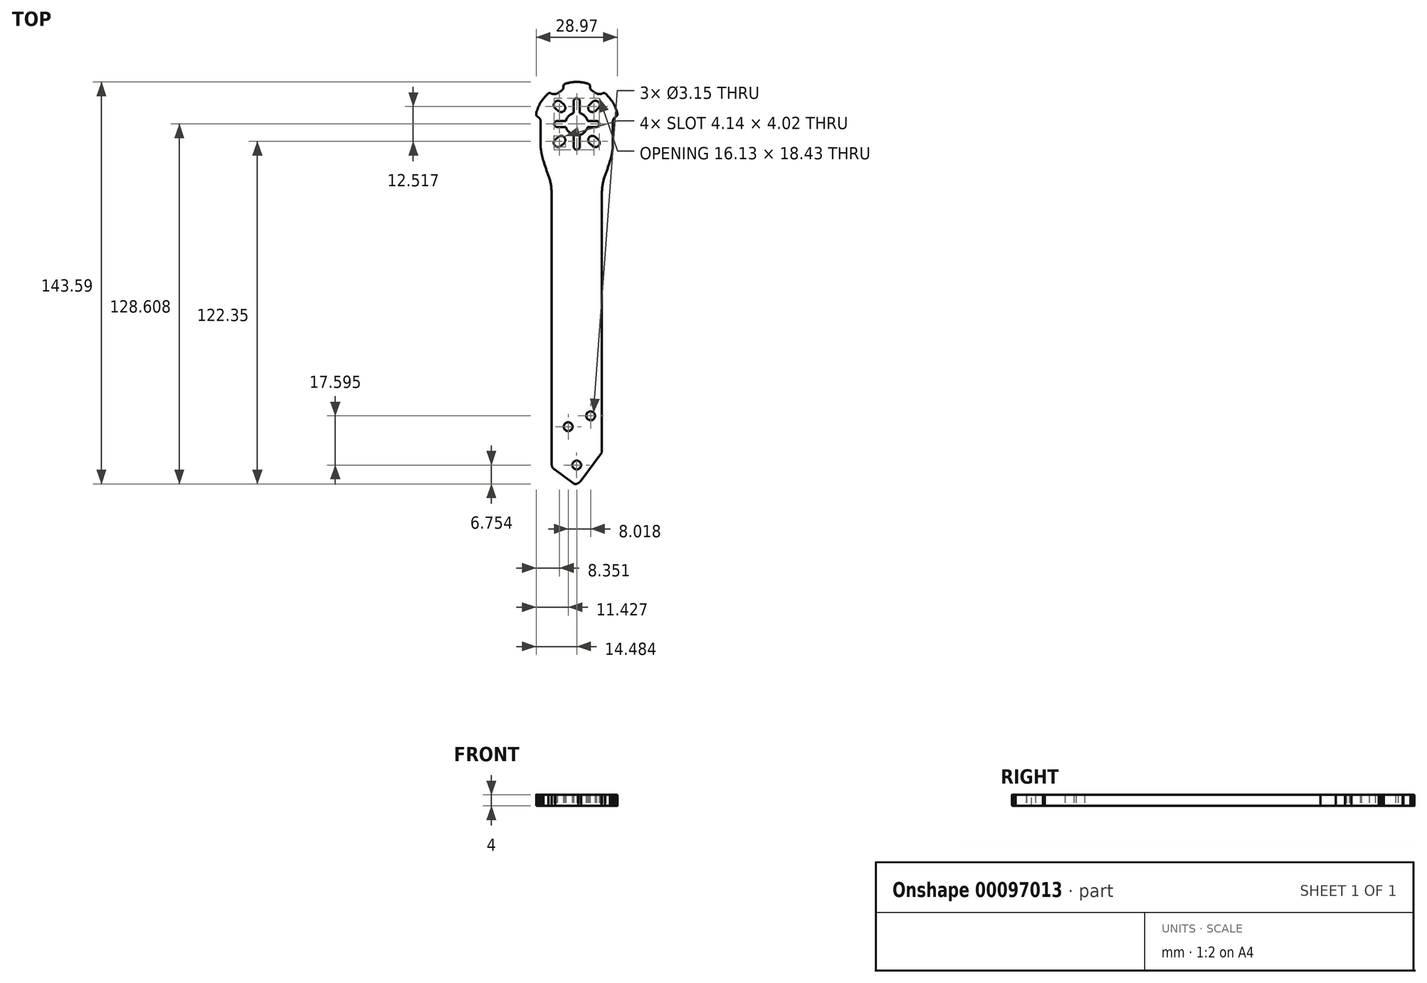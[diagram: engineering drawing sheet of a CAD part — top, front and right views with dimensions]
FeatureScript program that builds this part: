
annotation { "Feature Type Name" : "Feature", "Feature Type Description" : "" }
export const myFeature = defineFeature(function(context is Context, id is Id, definition is map)
    precondition{}
    {
        {
            var Q0;
            Q0=qCreatedBy(makeId("Top.planeOp"),FACE);
            var sketch = newSketch(context, id + "F0", { "sketchPlane" : qUnion([Q0])});
            skCircle(sketch, "E0", {"center": v(-4.22, -64.34) * mm, "radius": 1.57 * mm});
            skCircle(sketch, "E1", {"center": v(-12.24, -68.23) * mm, "radius": 1.57 * mm});
            skCircle(sketch, "E2", {"center": v(-9.2, -81.94) * mm, "radius": 1.57 * mm});
            skArc(sketch, "E3", {"start": v(-5.3, 41) * mm, "mid": v(-6.34, 42.79) * mm, "end": v(-8.13, 43.83) * mm});
            skArc(sketch, "E4", {"start": v(-1.12, 39.92) * mm, "mid": v(-1.4, 40.66) * mm, "end": v(-2.13, 41) * mm});
            skArc(sketch, "E5", {"start": v(-8.13, 48.05) * mm, "mid": v(-8.45, 48.82) * mm, "end": v(-9.22, 49.13) * mm});
            skLineSegment(sketch, "E6", {"start": v(-2.13, 41) * mm, "end": v(-5.3, 41) * mm});
            skLineSegment(sketch, "E7", {"start": v(-8.13, 48.05) * mm, "end": v(-8.13, 43.83) * mm});
            skLineSegment(sketch, "E8", {"start": v(-2.16, 45.18) * mm, "end": v(-2.16, 45.18) * mm});
            skArc(sketch, "E9", {"start": v(-4.61, 46.83) * mm, "mid": v(-4.74, 44.68) * mm, "end": v(-2.58, 44.55) * mm});
            skLineSegment(sketch, "E10", {"start": v(-3.52, 47.8) * mm, "end": v(-4.61, 46.83) * mm});
            skLineSegment(sketch, "E11", {"start": v(-2.58, 44.55) * mm, "end": v(-1.5, 45.52) * mm});
            skArc(sketch, "E12.trimOffspring", {"start": v(-1.5, 45.52) * mm, "mid": v(-1.37, 47.68) * mm, "end": v(-3.52, 47.8) * mm});
            skArc(sketch, "E13.MirrorCS", {"start": v(-1.5, 34.31) * mm, "mid": v(-1.37, 32.16) * mm, "end": v(-3.52, 32.03) * mm});
            skLineSegment(sketch, "E14.MirrorCS", {"start": v(-3.52, 32.03) * mm, "end": v(-4.61, 33) * mm});
            skArc(sketch, "E15.MirrorCS", {"start": v(-4.61, 33) * mm, "mid": v(-4.74, 35.16) * mm, "end": v(-2.58, 35.29) * mm});
            skLineSegment(sketch, "E16.MirrorCS", {"start": v(-2.58, 35.29) * mm, "end": v(-1.5, 34.31) * mm});
            skArc(sketch, "E17.MirrorCS", {"start": v(-1.12, 39.92) * mm, "mid": v(-1.4, 39.18) * mm, "end": v(-2.13, 38.84) * mm});
            skLineSegment(sketch, "E18.MirrorCS", {"start": v(-8.13, 31.79) * mm, "end": v(-8.13, 36) * mm});
            skLineSegment(sketch, "E19.MirrorCS", {"start": v(-2.13, 38.84) * mm, "end": v(-5.3, 38.84) * mm});
            skArc(sketch, "E20.MirrorCS", {"start": v(-5.3, 38.84) * mm, "mid": v(-6.34, 37.05) * mm, "end": v(-8.13, 36) * mm});
            skArc(sketch, "E21.MirrorCS", {"start": v(-8.13, 31.79) * mm, "mid": v(-8.45, 31.02) * mm, "end": v(-9.22, 30.7) * mm});
            skArc(sketch, "E22", {"start": v(0.93, 21.46) * mm, "mid": v(0.09, 18.5) * mm, "end": v(-0.19, 15.46) * mm});
            skArc(sketch, "E23", {"start": v(0.93, 21.46) * mm, "mid": v(1.86, 24.11) * mm, "end": v(2.71, 26.8) * mm});
            skArc(sketch, "E24", {"start": v(2.71, 26.8) * mm, "mid": v(3.17, 28.42) * mm, "end": v(3.5, 30.09) * mm});
            skArc(sketch, "E25", {"start": v(3.5, 30.09) * mm, "mid": v(3.66, 31.29) * mm, "end": v(3.74, 32.5) * mm});
            skLineSegment(sketch, "E26", {"start": v(3.74, 32.5) * mm, "end": v(3.74, 40.9) * mm});
            skArc(sketch, "E27", {"start": v(4.33, 42.17) * mm, "mid": v(3.9, 41.6) * mm, "end": v(3.74, 40.9) * mm});
            skArc(sketch, "E28", {"start": v(4.95, 42.62) * mm, "mid": v(4.64, 42.4) * mm, "end": v(4.33, 42.17) * mm});
            skArc(sketch, "E29", {"start": v(4.95, 42.62) * mm, "mid": v(5.2, 42.9) * mm, "end": v(5.3, 43.27) * mm});
            skArc(sketch, "E30", {"start": v(5.3, 43.27) * mm, "mid": v(5.28, 43.63) * mm, "end": v(5.2, 43.98) * mm});
            skArc(sketch, "E31", {"start": v(5.2, 43.98) * mm, "mid": v(3.66, 47.64) * mm, "end": v(1.1, 50.68) * mm});
            skArc(sketch, "E32", {"start": v(1.1, 50.68) * mm, "mid": v(0.6, 50.95) * mm, "end": v(0.04, 50.85) * mm});
            skArc(sketch, "E33", {"start": v(-2.22, 50.85) * mm, "mid": v(-1.09, 50.55) * mm, "end": v(0.04, 50.85) * mm});
            skArc(sketch, "E34", {"start": v(-4.01, 52.04) * mm, "mid": v(-3.15, 51.4) * mm, "end": v(-2.22, 50.85) * mm});
            skArc(sketch, "E35", {"start": v(-4.39, 52.76) * mm, "mid": v(-4.27, 52.36) * mm, "end": v(-4.01, 52.04) * mm});
            skArc(sketch, "E36", {"start": v(-4.45, 53.55) * mm, "mid": v(-4.42, 53.15) * mm, "end": v(-4.39, 52.76) * mm});
            skArc(sketch, "E37", {"start": v(-4.45, 53.55) * mm, "mid": v(-4.62, 53.95) * mm, "end": v(-4.96, 54.22) * mm});
            skArc(sketch, "E38", {"start": v(-4.96, 54.22) * mm, "mid": v(-7.06, 54.75) * mm, "end": v(-9.22, 54.9) * mm});
            skArc(sketch, "E39", {"start": v(-18.19, -81.72) * mm, "mid": v(-17.77, -82.83) * mm, "end": v(-16.92, -83.66) * mm});
            skLineSegment(sketch, "E40", {"start": v(-16.92, -83.66) * mm, "end": v(-10.54, -88.38) * mm});
            skArc(sketch, "E41", {"start": v(-10.54, -88.38) * mm, "mid": v(-9.6, -88.7) * mm, "end": v(-8.66, -88.38) * mm});
            skArc(sketch, "E42", {"start": v(-8.66, -88.38) * mm, "mid": v(-8.1, -87.97) * mm, "end": v(-7.64, -87.45) * mm});
            skLineSegment(sketch, "E43", {"start": v(-7.64, -87.45) * mm, "end": v(-0.42, -77.68) * mm});
            skArc(sketch, "E44", {"start": v(-0.42, -77.68) * mm, "mid": v(-0.26, -77.4) * mm, "end": v(-0.19, -77.07) * mm});
            skPoint(sketch, "E45", {"position": v(-9.19, 15.46) * mm});
            skLineSegment(sketch, "E46", {"start": v(-9.19, 54.9) * mm, "end": v(-9.19, -88.64) * mm});
            skArc(sketch, "E47.MirrorCS", {"start": v(-13.4, 54.22) * mm, "mid": v(-11.31, 54.75) * mm, "end": v(-9.15, 54.9) * mm});
            skArc(sketch, "E48.MirrorCS", {"start": v(-13.92, 53.55) * mm, "mid": v(-13.75, 53.95) * mm, "end": v(-13.4, 54.22) * mm});
            skArc(sketch, "E49.MirrorCS", {"start": v(-13.92, 53.55) * mm, "mid": v(-13.95, 53.15) * mm, "end": v(-13.98, 52.76) * mm});
            skArc(sketch, "E50.MirrorCS", {"start": v(-13.98, 52.76) * mm, "mid": v(-14.1, 52.36) * mm, "end": v(-14.36, 52.04) * mm});
            skArc(sketch, "E51.MirrorCS", {"start": v(-14.36, 52.04) * mm, "mid": v(-15.22, 51.4) * mm, "end": v(-16.16, 50.85) * mm});
            skArc(sketch, "E52.MirrorCS", {"start": v(-16.16, 50.85) * mm, "mid": v(-17.29, 50.55) * mm, "end": v(-18.42, 50.85) * mm});
            skArc(sketch, "E53.MirrorCS", {"start": v(-19.48, 50.68) * mm, "mid": v(-18.98, 50.95) * mm, "end": v(-18.42, 50.85) * mm});
            skArc(sketch, "E54.MirrorCS", {"start": v(-23.57, 43.98) * mm, "mid": v(-22.03, 47.64) * mm, "end": v(-19.48, 50.68) * mm});
            skArc(sketch, "E55.MirrorCS", {"start": v(-16.88, 45.52) * mm, "mid": v(-17, 47.68) * mm, "end": v(-14.85, 47.8) * mm});
            skLineSegment(sketch, "E56.MirrorCS", {"start": v(-14.85, 47.8) * mm, "end": v(-13.76, 46.83) * mm});
            skArc(sketch, "E57.MirrorCS", {"start": v(-13.76, 46.83) * mm, "mid": v(-13.63, 44.68) * mm, "end": v(-15.79, 44.55) * mm});
            skLineSegment(sketch, "E58.MirrorCS", {"start": v(-15.79, 44.55) * mm, "end": v(-16.88, 45.52) * mm});
            skArc(sketch, "E59.MirrorCS", {"start": v(-10.24, 48.05) * mm, "mid": v(-9.92, 48.82) * mm, "end": v(-9.15, 49.13) * mm});
            skLineSegment(sketch, "E60.MirrorCS", {"start": v(-10.24, 48.05) * mm, "end": v(-10.24, 43.83) * mm});
            skArc(sketch, "E61.MirrorCS", {"start": v(-23.67, 43.27) * mm, "mid": v(-23.65, 43.63) * mm, "end": v(-23.57, 43.98) * mm});
            skArc(sketch, "E62.MirrorCS", {"start": v(-23.32, 42.62) * mm, "mid": v(-23.57, 42.9) * mm, "end": v(-23.67, 43.27) * mm});
            skArc(sketch, "E63.MirrorCS", {"start": v(-23.32, 42.62) * mm, "mid": v(-23, 42.4) * mm, "end": v(-22.7, 42.17) * mm});
            skArc(sketch, "E64.MirrorCS", {"start": v(-22.7, 42.17) * mm, "mid": v(-22.27, 41.6) * mm, "end": v(-22.11, 40.9) * mm});
            skLineSegment(sketch, "E65.MirrorCS", {"start": v(-22.11, 32.5) * mm, "end": v(-22.11, 40.9) * mm});
            skArc(sketch, "E66.MirrorCS", {"start": v(-13.07, 41) * mm, "mid": v(-12.03, 42.79) * mm, "end": v(-10.24, 43.83) * mm});
            skLineSegment(sketch, "E67.MirrorCS", {"start": v(-16.25, 41) * mm, "end": v(-13.07, 41) * mm});
            skArc(sketch, "E68.MirrorCS", {"start": v(-17.25, 39.92) * mm, "mid": v(-16.96, 40.66) * mm, "end": v(-16.25, 41) * mm});
            skArc(sketch, "E69.MirrorCS", {"start": v(-17.25, 39.92) * mm, "mid": v(-16.96, 39.18) * mm, "end": v(-16.25, 38.84) * mm});
            skLineSegment(sketch, "E70.MirrorCS", {"start": v(-16.25, 38.84) * mm, "end": v(-13.07, 38.84) * mm});
            skArc(sketch, "E71.MirrorCS", {"start": v(-13.07, 38.84) * mm, "mid": v(-12.03, 37.05) * mm, "end": v(-10.24, 36) * mm});
            skLineSegment(sketch, "E72.MirrorCS", {"start": v(-10.24, 31.79) * mm, "end": v(-10.24, 36) * mm});
            skArc(sketch, "E73.MirrorCS", {"start": v(-10.24, 31.79) * mm, "mid": v(-9.92, 31.02) * mm, "end": v(-9.15, 30.7) * mm});
            skArc(sketch, "E74.MirrorCS", {"start": v(-13.76, 33) * mm, "mid": v(-13.63, 35.16) * mm, "end": v(-15.79, 35.29) * mm});
            skLineSegment(sketch, "E75.MirrorCS", {"start": v(-15.79, 35.29) * mm, "end": v(-16.88, 34.31) * mm});
            skArc(sketch, "E76.MirrorCS", {"start": v(-16.88, 34.31) * mm, "mid": v(-17, 32.16) * mm, "end": v(-14.85, 32.03) * mm});
            skLineSegment(sketch, "E77.MirrorCS", {"start": v(-14.85, 32.03) * mm, "end": v(-13.76, 33) * mm});
            skArc(sketch, "E78.MirrorCS", {"start": v(-21.87, 30.09) * mm, "mid": v(-22.04, 31.29) * mm, "end": v(-22.11, 32.5) * mm});
            skArc(sketch, "E79.MirrorCS", {"start": v(-21.08, 26.8) * mm, "mid": v(-21.55, 28.42) * mm, "end": v(-21.87, 30.09) * mm});
            skArc(sketch, "E80.MirrorCS", {"start": v(-19.3, 21.46) * mm, "mid": v(-20.23, 24.11) * mm, "end": v(-21.08, 26.8) * mm});
            skArc(sketch, "E81.MirrorCS", {"start": v(-19.3, 21.46) * mm, "mid": v(-18.46, 18.5) * mm, "end": v(-18.19, 15.46) * mm});
            skLineSegment(sketch, "E82", {"start": v(-12.24, -68.23) * mm, "end": v(-9.19, -68.23) * mm});
            skLineSegment(sketch, "E83", {"start": v(-4.22, -64.34) * mm, "end": v(-9.19, -64.34) * mm});
            skLineSegment(sketch, "E84.trimOffspring", {"start": v(-18.19, 15.46) * mm, "end": v(-18.19, 15.46) * mm});
            skLineSegment(sketch, "E85", {"start": v(-18.19, 15.46) * mm, "end": v(-18.19, -81.73) * mm});
            skLineSegment(sketch, "E86", {"start": v(-0.19, 15.46) * mm, "end": v(-0.19, -77.07) * mm});
            skLineSegment(sketch, "E87", {"start": v(-0.19, -55.55) * mm, "end": v(-18.19, -55.55) * mm});
            skLineSegment(sketch, "E88", {"start": v(-0.19, 3.48) * mm, "end": v(-18.19, 3.48) * mm});
            skLineSegment(sketch, "E89", {"start": v(-0.19, 13.23) * mm, "end": v(-18.19, 13.23) * mm});
            skSolve(sketch);
        }
        {
            var Q0;
            Q0 = qSketchRegion(id + "F0", true);
            extrude(context, id + "F1", {"entities" : qUnion([Q0]), "depth" : 4 * mm});
        }
    });
